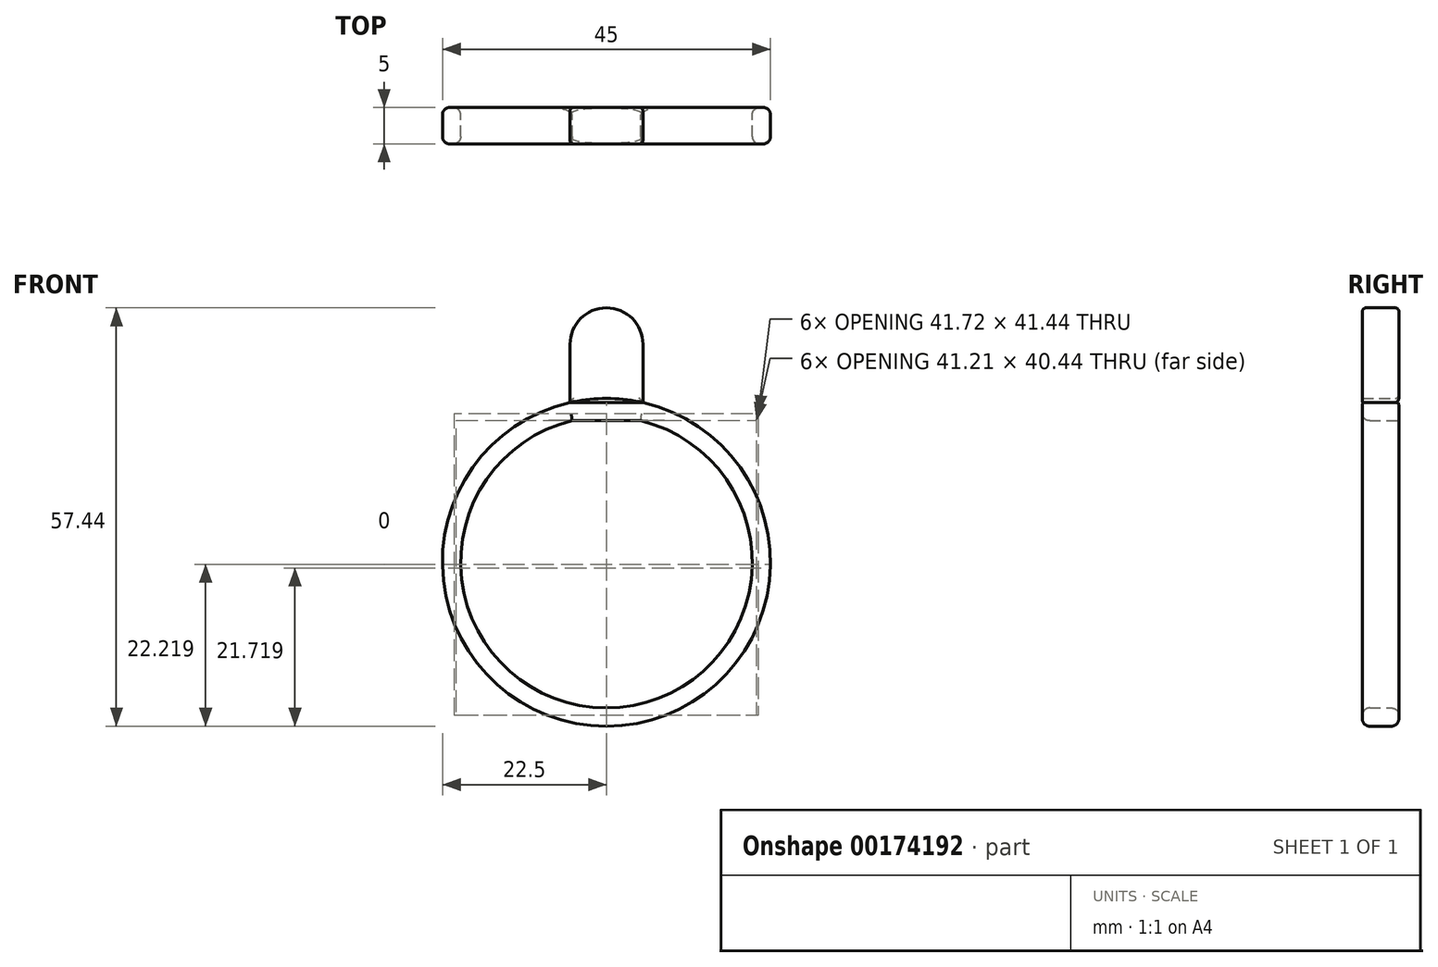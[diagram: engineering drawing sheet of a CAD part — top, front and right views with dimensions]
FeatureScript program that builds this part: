
annotation { "Feature Type Name" : "Feature", "Feature Type Description" : "" }
export const myFeature = defineFeature(function(context is Context, id is Id, definition is map)
    precondition{}
    {
        {
            var Q0;
            Q0=qCreatedBy(makeId("Front.planeOp"),FACE);
            var sketch = newSketch(context, id + "F0", { "sketchPlane" : qUnion([Q0])});
            skCircle(sketch, "E0", {"center": v(0, 0) * mm, "radius": 22.5 * mm});
            skLineSegment(sketch, "E1.bottom", {"start": v(5, 21.94) * mm, "end": v(-5, 21.94) * mm});
            skLineSegment(sketch, "E1.top", {"start": v(5, 29.94) * mm, "end": v(-5, 29.94) * mm});
            skLineSegment(sketch, "E1.left", {"start": v(5, 21.94) * mm, "end": v(5, 29.94) * mm});
            skLineSegment(sketch, "E1.right", {"start": v(-5, 21.94) * mm, "end": v(-5, 29.94) * mm});
            skPoint(sketch, "E1.middle", {"position": v(0, 25.94) * mm});
            skArc(sketch, "E2", {"start": v(5, 29.94) * mm, "mid": v(0, 34.94) * mm, "end": v(-5, 29.94) * mm});
            skSolve(sketch);
        }
        {
            var Q0;
            {var subQ0=sQuery(id+"F0.wireOp",EDGE,"E1.bottom");Q0=makeQuery(id+"F0.imprint","IMPRINT",FACE,{"disambiguationData":[TD([[makeQuery(id+"F0.imprint","IMPRINT",EDGE,{"derivedFrom":subQ0}),1.0]])]});}
            var Q1;
            Q1=makeQuery(id+"F0.imprint","IMPRINT",FACE,{"disambiguationData":[TD([[makeQuery(id+"F0.imprint","IMPRINT",EDGE,{"derivedFrom":sQuery(id+"F0.wireOp",EDGE,"E1.top")}),1.0]])]});
            var Q2;
            Q2=makeQuery(id+"F0.imprint","IMPRINT",FACE,{"disambiguationData":[TD([[makeQuery(id+"F0.imprint","IMPRINT",EDGE,{"derivedFrom":sQuery(id+"F0.wireOp",EDGE,"E1.top")}),-1.0]])]});
            extrude(context, id + "F1", {"entities" : qUnion([Q0, Q1, Q2]), "depth" : 5 * mm});
        }
        {
            var Q0;
            Q0=makeQuery(id+"F1.opExtrude","CAP_FACE",FACE,{"disambiguationData":[OSD([sQuery(id+"F0.wireOp",EDGE,"E0"),sQuery(id+"F0.wireOp",EDGE,"E1.bottom")])],"isStart":true});
            var Q1;
            Q1=makeQuery(id+"F1.opExtrude","CAP_FACE",FACE,{"disambiguationData":[OSD([sQuery(id+"F0.wireOp",EDGE,"E0"),sQuery(id+"F0.wireOp",EDGE,"E1.bottom")])],"isStart":false});
            shell(context, id + "F2", {"entities" : qUnion([Q0, Q1]), "thickness" : 2.5 * mm});
        }
        {
            var Q0;
            {var subQ0=sQuery(id+"F0.wireOp",EDGE,"E1.bottom");var subQ1=sQuery(id+"F0.wireOp",EDGE,"E0");Q0=makeQuery(id+"F2.opShell","OFFSET_EDGE",EDGE,{"disambiguationData":[OSD([subQ1]),TDD([makeQuery(id+"F1.opExtrude","CAP_EDGE",EDGE,{"disambiguationData":[OSD([subQ1]),TDD([makeQuery(id+"F0.imprint","IMPRINT",EDGE,{"disambiguationData":[TD([[makeQuery(id+"F0.imprint","INTERSECT",VERTEX,{"derivedFrom":[subQ1,subQ0,sQuery(id+"F0.wireOp",EDGE,"E1.left")]}),1.0]])],"derivedFrom":subQ1})])],"isStart":true})])]});}
            var Q1;
            {var subQ0=sQuery(id+"F0.wireOp",EDGE,"E1.bottom");var subQ1=sQuery(id+"F0.wireOp",EDGE,"E0");Q1=makeQuery(id+"F2.opShell","OFFSET_EDGE",EDGE,{"disambiguationData":[OSD([subQ1]),TDD([makeQuery(id+"F1.opExtrude","CAP_EDGE",EDGE,{"disambiguationData":[OSD([subQ1]),TDD([makeQuery(id+"F0.imprint","IMPRINT",EDGE,{"disambiguationData":[TD([[makeQuery(id+"F0.imprint","INTERSECT",VERTEX,{"derivedFrom":[subQ1,subQ0,sQuery(id+"F0.wireOp",EDGE,"E1.left")]}),1.0]])],"derivedFrom":subQ1})])],"isStart":false})])]});}
            var Q2;
            {var subQ0=sQuery(id+"F0.wireOp",EDGE,"E1.bottom");var subQ1=sQuery(id+"F0.wireOp",EDGE,"E0");Q2=makeQuery(id+"F1.opExtrude","CAP_EDGE",EDGE,{"disambiguationData":[OSD([subQ1]),TDD([makeQuery(id+"F0.imprint","IMPRINT",EDGE,{"disambiguationData":[TD([[makeQuery(id+"F0.imprint","INTERSECT",VERTEX,{"derivedFrom":[subQ1,subQ0,sQuery(id+"F0.wireOp",EDGE,"E1.left")]}),1.0]])],"derivedFrom":subQ1})])],"isStart":false});}
            var Q3;
            {var subQ0=sQuery(id+"F0.wireOp",EDGE,"E1.bottom");Q3=makeQuery(id+"F2.opShell","OFFSET_EDGE",EDGE,{"disambiguationData":[OSD([subQ0]),TDD([makeQuery(id+"F1.opExtrude","CAP_EDGE",EDGE,{"disambiguationData":[OSD([subQ0])],"isStart":false})])]});}
            var Q4;
            {var subQ0=sQuery(id+"F0.wireOp",EDGE,"E1.bottom");var subQ1=sQuery(id+"F0.wireOp",EDGE,"E0");Q4=makeQuery(id+"F1.opExtrude","CAP_EDGE",EDGE,{"disambiguationData":[OSD([subQ1]),TDD([makeQuery(id+"F0.imprint","IMPRINT",EDGE,{"disambiguationData":[TD([[makeQuery(id+"F0.imprint","INTERSECT",VERTEX,{"derivedFrom":[subQ1,subQ0,sQuery(id+"F0.wireOp",EDGE,"E1.left")]}),1.0]])],"derivedFrom":subQ1})])],"isStart":true});}
            fillet(context, id + "F3", {"entities" : qUnion([Q0, Q1, Q2, Q3, Q4]), "radius" : 1 * mm, "tangentPropagation" : true, "allowEdgeOverflow" : false});
        }
        {
            var Q0;
            Q0=makeQuery(id+"F1.opExtrude","CAP_EDGE",EDGE,{"disambiguationData":[OSD([sQuery(id+"F0.wireOp",EDGE,"E1.left")])],"isStart":false});
            var Q1;
            Q1=makeQuery(id+"F1.opExtrude","CAP_EDGE",EDGE,{"disambiguationData":[OSD([sQuery(id+"F0.wireOp",EDGE,"E2")])],"isStart":false});
            var Q2;
            Q2=makeQuery(id+"F1.opExtrude","CAP_EDGE",EDGE,{"disambiguationData":[OSD([sQuery(id+"F0.wireOp",EDGE,"E1.right")])],"isStart":false});
            var Q3;
            Q3=makeQuery(id+"F1.opExtrude","CAP_EDGE",EDGE,{"disambiguationData":[OSD([sQuery(id+"F0.wireOp",EDGE,"E2")])],"isStart":true});
            var Q4;
            Q4=makeQuery(id+"F1.opExtrude","CAP_EDGE",EDGE,{"disambiguationData":[OSD([sQuery(id+"F0.wireOp",EDGE,"E1.right")])],"isStart":true});
            var Q5;
            Q5=makeQuery(id+"F1.opExtrude","CAP_EDGE",EDGE,{"disambiguationData":[OSD([sQuery(id+"F0.wireOp",EDGE,"E1.left")])],"isStart":true});
            var Q6;
            {var subQ0=sQuery(id+"F0.wireOp",EDGE,"E1.bottom");var subQ1=sQuery(id+"F0.wireOp",EDGE,"E0");Q6=makeQuery(id+"F1.opExtrude","CAP_EDGE",EDGE,{"disambiguationData":[OSD([subQ1]),TDD([makeQuery(id+"F0.imprint","IMPRINT",EDGE,{"disambiguationData":[TD([[makeQuery(id+"F0.imprint","INTERSECT",VERTEX,{"derivedFrom":[subQ1,subQ0,sQuery(id+"F0.wireOp",EDGE,"E1.left")]}),-1.0]])],"derivedFrom":subQ1})])],"isStart":true});}
            fillet(context, id + "F4", {"entities" : qUnion([Q0, Q1, Q2, Q3, Q4, Q5, Q6]), "radius" : .5 * mm, "tangentPropagation" : true, "allowEdgeOverflow" : false});
        }
    });
